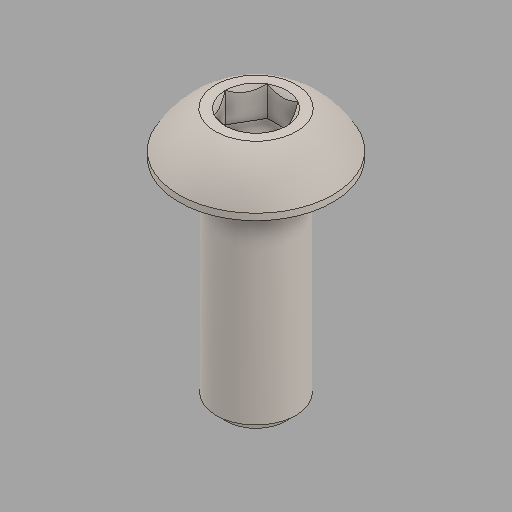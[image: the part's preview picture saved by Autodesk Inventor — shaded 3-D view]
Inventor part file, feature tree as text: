
AUTODESK INVENTOR PART (.ipt)
format: ipt  version: 2024.2 (Build 282272000, 272)  size: 132,608 bytes
history: native  units: in
note: dims shown in document units (in); Inventor stores cm internally (conversion verified against a paired STEP export)
features: fillet x1
ambient origin geometry x8: Origin, YZ Plane, XZ Plane, XY Plane, X Axis, Y Axis, Z Axis, Center Point
bodies: Solid1 (feature_tree)
feature tree (1):
  fillet  "Fillet1"  [1 undecoded]
note: 1 required parameter value undecoded (feature->parameter linkage not recoverable at this tier; creation-order binding heuristic only, values carry confidence <= 0.55)
